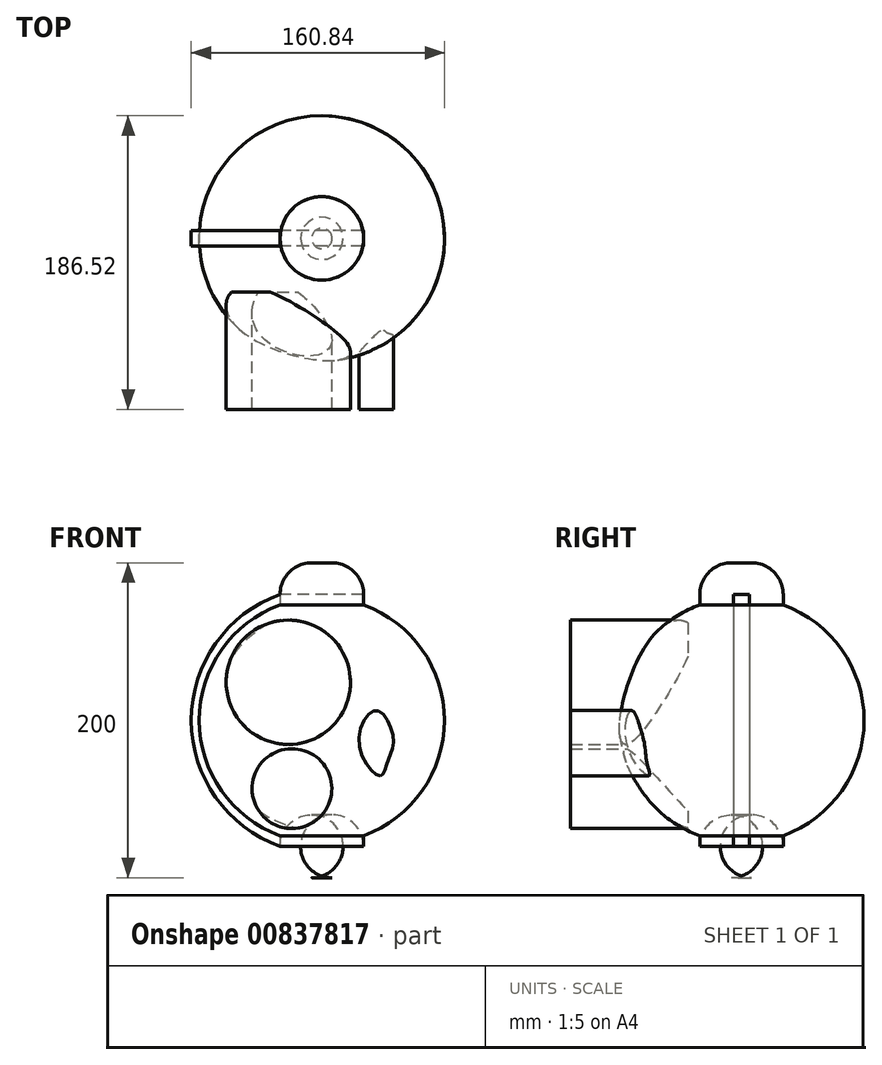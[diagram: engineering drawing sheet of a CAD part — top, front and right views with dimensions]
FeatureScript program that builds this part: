
annotation { "Feature Type Name" : "Feature", "Feature Type Description" : "" }
export const myFeature = defineFeature(function(context is Context, id is Id, definition is map)
    precondition{}
    {
        {
            var Q0;
            Q0=qCreatedBy(makeId("Top.planeOp"),FACE);
            var sketch = newSketch(context, id + "F0", { "sketchPlane" : qUnion([Q0])});
            skCircle(sketch, "E0", {"center": v(0, 0) * mm, "radius": 26.52 * mm});
            skCircle(sketch, "E1", {"center": v(0, 0) * mm, "radius": 77.92 * mm});
            skLineSegment(sketch, "E2", {"start": v(0, 0) * mm, "end": v(0, -77.92) * mm});
            skLineSegment(sketch, "E3", {"start": v(0, -77.92) * mm, "end": v(0, 77.92) * mm});
            skSolve(sketch);
        }
        {
            var Q0;
            {var subQ0=sQuery(id+"F0.wireOp",EDGE,"E3");var subQ1=sQuery(id+"F0.wireOp",EDGE,"E0");var subQ2=makeQuery(id+"F0.imprint","INTERSECT",VERTEX,{"disambiguationData":[OD(0.0)],"derivedFrom":[subQ1,subQ0]});Q0=makeQuery(id+"F0.imprint","IMPRINT",FACE,{"disambiguationData":[TD([[makeQuery(id+"F0.imprint","IMPRINT",EDGE,{"disambiguationData":[TD([[subQ2,-1.0]])],"derivedFrom":subQ1}),-1.0]])]});}
            var Q1;
            {var subQ0=sQuery(id+"F0.wireOp",EDGE,"E3");var subQ4=makeQuery(id+"F0.imprint","IMPRINT",VERTEX,{"derivedFrom":subQ0});Q1=makeQuery(id+"F0.imprint","IMPRINT",FACE,{"disambiguationData":[TD([[makeQuery(id+"F0.imprint","IMPRINT",EDGE,{"disambiguationData":[TD([[subQ4,1.0]])],"derivedFrom":subQ0}),-1.0]])]});}
            var Q2;
            Q2=sQuery(id+"F0.wireOp",EDGE,"E3");
            revolve(context, id + "F1", {"surfaceOperationType" : NewSurfaceOperationType.NEW, "entities" : qUnion([Q0, Q1]), "axis" : qUnion([Q2]), "revolveType" : RevolveType.FULL});
        }
        {
            var Q0;
            Q0=qCreatedBy(makeId("Top.planeOp"),FACE);
            var sketch = newSketch(context, id + "F2", { "sketchPlane" : qUnion([Q0])});
            skCircle(sketch, "E4.0", {"center": v(0, 0) * mm, "radius": 26.52 * mm});
            skSolve(sketch);
        }
        {
            var Q0;
            Q0 = qSketchRegion(id + "F2", true);
            extrude(context, id + "F3", {"entities" : qUnion([Q0]), "operationType" : NewBodyOperationType.ADD, "depth" : 100 * mm, "offsetDistance" : 25 * mm, "hasSecondDirection" : true, "secondDirectionOppositeDirection" : true, "secondDirectionDepth" : 100 * mm});
        }
        {
            var Q0;
            Q0=makeQuery(id+"F3.opExtrude","CAP_FACE",FACE,{"disambiguationData":[OSD([sQuery(id+"F2.wireOp",EDGE,"E4.0")])],"isStart":true});
            fillet(context, id + "F4", {"entities" : qUnion([Q0]), "radius" : 20 * mm, "tangentPropagation" : true, "allowEdgeOverflow" : false});
        }
        {
            var Q0;
            Q0=makeQuery(id+"F3.opExtrude","CAP_EDGE",EDGE,{"disambiguationData":[OSD([sQuery(id+"F2.wireOp",EDGE,"E4.0")])],"isStart":false});
            fillet(context, id + "F5", {"entities" : qUnion([Q0]), "radius" : 20 * mm, "tangentPropagation" : true, "allowEdgeOverflow" : false});
        }
        {
            var Q0;
            Q0=qCreatedBy(makeId("Front.planeOp"),FACE);
            var sketch = newSketch(context, id + "F6", { "sketchPlane" : qUnion([Q0])});
            skLineSegment(sketch, "E5.0", {"start": v(-77.92, 0) * mm, "end": v(77.92, 0) * mm});
            skLineSegment(sketch, "E5.1", {"start": v(-26.52, 0) * mm, "end": v(26.52, 0) * mm});
            skLineSegment(sketch, "E5.2", {"start": v(-77.92, 0) * mm, "end": v(77.92, 0) * mm});
            skLineSegment(sketch, "E5.3", {"start": v(-26.52, -80) * mm, "end": v(26.52, -80) * mm});
            skLineSegment(sketch, "E5.4", {"start": v(26.52, 73.26) * mm, "end": v(-26.52, 73.26) * mm});
            skLineSegment(sketch, "E5.5", {"start": v(6.52, -100) * mm, "end": v(-6.52, -100) * mm});
            skLineSegment(sketch, "E5.6", {"start": v(-26.52, -73.26) * mm, "end": v(26.52, -73.26) * mm});
            skLineSegment(sketch, "E5.7", {"start": v(26.52, 80) * mm, "end": v(-26.52, 80) * mm});
            skLineSegment(sketch, "E5.8", {"start": v(0, 0) * mm, "end": v(-77.92, 0) * mm});
            skArc(sketch, "E6", {"start": v(-26.52, 73.26) * mm, "mid": v(-77.92, 0) * mm, "end": v(-26.52, -73.26) * mm});
            skLineSegment(sketch, "E7", {"start": v(-77.92, 0) * mm, "end": v(-82.92, 0) * mm});
            skArc(sketch, "E8", {"start": v(-26.52, 80) * mm, "mid": v(-82.92, 0) * mm, "end": v(-26.52, -80) * mm});
            skLineSegment(sketch, "E9", {"start": v(26.52, -80) * mm, "end": v(26.52, -73.26) * mm});
            skLineSegment(sketch, "E10", {"start": v(26.52, 80) * mm, "end": v(26.52, 73.26) * mm});
            skSolve(sketch);
        }
        {
            var Q0;
            {var subQ3=sQuery(id+"F6.wireOp",EDGE,"E5.3");Q0=makeQuery(id+"F6.imprint","IMPRINT",FACE,{"disambiguationData":[TD([[makeQuery(id+"F6.imprint","IMPRINT",EDGE,{"derivedFrom":subQ3}),1.0]])]});}
            var Q1;
            {var subQ2=sQuery(id+"F6.wireOp",EDGE,"E5.4");Q1=makeQuery(id+"F6.imprint","IMPRINT",FACE,{"disambiguationData":[TD([[makeQuery(id+"F6.imprint","IMPRINT",EDGE,{"derivedFrom":subQ2}),-1.0]])]});}
            extrude(context, id + "F7", {"entities" : qUnion([Q0, Q1]), "depth" : 5 * mm, "offsetDistance" : 25 * mm, "hasSecondDirection" : true, "secondDirectionOppositeDirection" : true, "secondDirectionDepth" : 5 * mm});
        }
        {
            var Q0;
            Q0=qCreatedBy(makeId("Front.planeOp"),FACE);
            cPlane(context, id + "F8", {"entities" : qUnion([Q0]), "cplaneType" : CPlaneType.OFFSET, "offset" : 34 * mm, "width" : 150 * mm, "height" : 150 * mm});
        }
        {
            var Q0;
            Q0=qCreatedBy(id+"F8.planeOp",FACE);
            var sketch = newSketch(context, id + "F9", { "sketchPlane" : qUnion([Q0])});
            skCircle(sketch, "E11", {"center": v(-18.98, -43.38) * mm, "radius": 25.33 * mm});
            skCircle(sketch, "E12", {"center": v(-21.3, 24.18) * mm, "radius": 39.47 * mm});
            skFitSpline(sketch, "E13", {"points": [v(37.13, -35.25) * mm, v(23.73, -15.12) * mm, v(34.5, 6.14) * mm, v(45.3, -11.35) * mm, v(41.33, -27.58) * mm, v(37.13, -35.25) * mm]});
            skSolve(sketch);
        }
        {
            var Q0;
            Q0 = qSketchRegion(id + "F9", true);
            extrude(context, id + "F10", {"entities" : qUnion([Q0]), "operationType" : NewBodyOperationType.ADD, "depth" : 74.6 * mm, "offsetDistance" : 25 * mm});
        }
    });
